# Revit family: LC11 Wood
name_source: partatom
category: Furniture
revit_build: Autodesk Revit 2016 (Build: 20160525_1230(x64)
units: mm (PartAtom-declared; Revit-internal decimal feet)

## family parameters
Always vertical = Yes
Cut with Voids When Loaded = No
OmniClass Number = 23.40.20.00
OmniClass Title = General Furniture and Specialties
Room Calculation Point = No
Shared = No
Work Plane-Based = No

## types (4) — shared parameters
Assembly Code = E2020200
Manufacturer = Gresham Office Furniture
Model = LC11 WOOD
Range = SEATING
URL = www.gof.co.uk

## per-type parameters (varying)
| type | LC11H1 | LC11H1 Seat | LC11H2 Seat | LC11J1 | LC11J1 Seat | LC11J2 Seat |
| LC11H1 | Yes | Yes | No | No | No | No |
| LC11J1 | No | No | No | Yes | Yes | No |
| LC11H2 | Yes | No | Yes | No | No | No |
| LC11J2 | No | No | No | Yes | No | Yes |

note: column(s) folded — value = type name in every type: Product Code

## geometry (parser evidence)
native form markers: Sweep x3
no freeform markers — native parametric forms only
